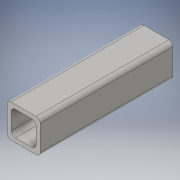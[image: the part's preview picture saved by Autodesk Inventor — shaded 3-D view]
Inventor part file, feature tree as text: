
AUTODESK INVENTOR PART (.ipt)
format: ipt  version: 2016 (Build 200138000, 138)  size: 112,640 bytes
history: native  units: in
note: dims shown in document units (in); Inventor stores cm internally (conversion verified against a paired STEP export)
features: extrude x1, sketch x1
ambient origin geometry x8: Origin, YZ Plane, XZ Plane, XY Plane, X Axis, Y Axis, Z Axis, Center Point
bodies: Solid1 (feature_tree)
feature tree (2):
  extrude  "Extrusion1"  Depth=1.0in
  sketch  "Sketch1"  dims[d0=1.0in d1=1.0in d2=0.125in d3=0.125in d4=4.0in d5=0.0in]
